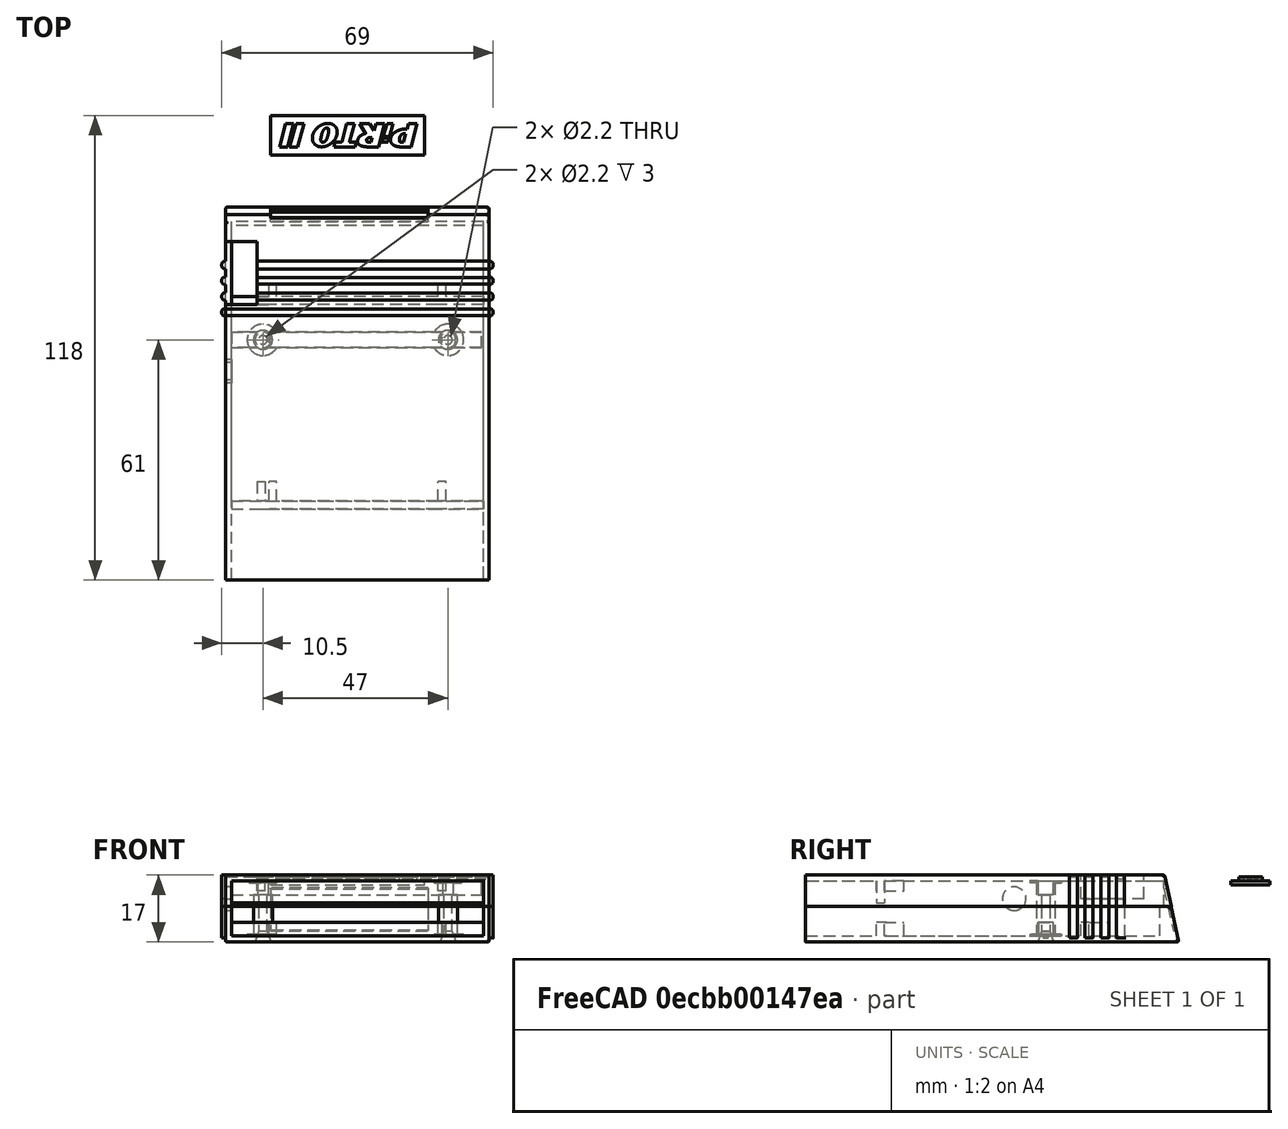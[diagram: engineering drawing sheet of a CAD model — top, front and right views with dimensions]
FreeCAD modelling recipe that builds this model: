
FCSTD DOCUMENT  (FreeCAD 0.21R33771 (Git))
Label: PiRTOII_Cart
License: All rights reserved
LicenseURL: http://en.wikipedia.org/wiki/All_rights_reserved
objects: Part::Cylinder×33, Part::MultiFuse×26, Part::Box×19, Part::Cut×17, Part::Fillet×8, Mesh::Feature×3, Part::Cone×2, Part::Part2DObjectPython×1, Part::Extrusion×1
note: 107 computed .brp shape members not serialized (recipe doc carries the construction recipe); baked Part::Feature solids carry a one-line shape summary decoded from their .brp

FEATURE [Part::Cylinder] Cylinder  label="Cilindro"
  Angle = 360
  AttacherType = Attacher::AttachEngine3D
  FirstAngle = 0
  Height = 1
  Placement = pos=(52.5,43,0) rot=(0,0,1;0rad)
  Radius = 4
  SecondAngle = 0
FEATURE [Part::Cylinder] Cylinder001  label="Cilindro001"
  Angle = 360
  AttacherType = Attacher::AttachEngine3D
  FirstAngle = 0
  Height = 1
  Placement = pos=(13.5,43,0) rot=(0,0,1;0rad)
  Radius = 4
  SecondAngle = 0
FEATURE [Part::Box] Box  label="Base_int"
  AttacherType = Attacher::AttachEngine3D
  Height = 10
  Length = 64
  Placement = pos=(1.5,0,0.5) rot=(0,0,1;0rad)
  Width = 90
FEATURE [Part::Box] Box001  label="Base_ext"
  AttacherType = Attacher::AttachEngine3D
  Height = 9
  Length = 67
  Placement = pos=(0,0,-1) rot=(0,0,1;0rad)
  Width = 95
FEATURE [Part::Cut] Cut  label="BaseVuota"
  Base = -> Box001
  Tool = -> Box
FEATURE [Part::Box] Box002  label="Cubo"
  AttacherType = Attacher::AttachEngine3D
  Height = 4
  Length = 66
  Placement = pos=(0,18,0) rot=(0,0,1;0rad)
  Width = 2
FEATURE [Part::Box] Box003  label="Cubo001"
  AttacherType = Attacher::AttachEngine3D
  Height = 4
  Length = 2
  Placement = pos=(11,18,0) rot=(0,0,1;0rad)
  Width = 7
FEATURE [Part::Box] Box004  label="Cubo002"
  AttacherType = Attacher::AttachEngine3D
  Height = 4
  Length = 2
  Placement = pos=(54,18,0) rot=(0,0,1;0rad)
  Width = 7
FEATURE [Part::MultiFuse] Fusion  label="Holder"
  Shapes = -> [Box004,Box003,Box002]
FEATURE [Part::Cylinder] Cylinder002  label="Cilindro002"
  Angle = 360
  AttacherType = Attacher::AttachEngine3D
  FirstAngle = 0
  Height = 8
  Placement = pos=(52.5,43,0) rot=(0,0,1;0rad)
  Radius = 2.4
  SecondAngle = 0
FEATURE [Part::Cylinder] Cylinder003  label="Cilindro003"
  Angle = 360
  AttacherType = Attacher::AttachEngine3D
  FirstAngle = 0
  Height = 8
  Placement = pos=(13.5,43,0) rot=(0,0,1;0rad)
  Radius = 2.4
  SecondAngle = 0
FEATURE [Part::MultiFuse] Fusion001
  Placement = pos=(-4,18,0) rot=(0,0,1;0rad)
  Shapes = -> [Cylinder003,Cylinder001]
FEATURE [Part::Box] Box005  label="apertura"
  AttacherType = Attacher::AttachEngine3D
  Height = 7
  Length = 18
  Placement = pos=(-10,70,10) rot=(0,0,1;0rad)
  Width = 16
FEATURE [Part::Cut] Cut001
  Base = -> Cut
  Tool = -> Box005
FEATURE [Part::Box] Box006  label="Taglio"
  AttacherType = Attacher::AttachEngine3D
  Height = 30
  Length = 72
  Placement = pos=(0,95,-2) rot=(1,0,0;0.20944rad)
  Width = 30
FEATURE [Part::Cut] Cut002  label="Base2"
  Base = -> Cut001
  Tool = -> Box006
FEATURE [Part::Cylinder] Cylinder004  label="Cyl1"
  Angle = 360
  AttacherType = Attacher::AttachEngine3D
  FirstAngle = 0
  Height = 8
  Placement = pos=(67,80,0) rot=(0,0,1;0rad)
  Radius = 1
  SecondAngle = 0
FEATURE [Part::Cylinder] Cylinder005  label="Cyl002"
  Angle = 360
  AttacherType = Attacher::AttachEngine3D
  FirstAngle = 0
  Height = 8
  Placement = pos=(67,84,0) rot=(0,0,1;0rad)
  Radius = 1
  SecondAngle = 0
FEATURE [Part::Cylinder] Cylinder006  label="Cyl003"
  Angle = 360
  AttacherType = Attacher::AttachEngine3D
  FirstAngle = 0
  Height = 8
  Placement = pos=(67,88,0) rot=(0,0,1;0rad)
  Radius = 1
  SecondAngle = 0
FEATURE [Part::Cylinder] Cylinder007  label="Cyl004"
  Angle = 360
  AttacherType = Attacher::AttachEngine3D
  FirstAngle = 0
  Height = 8
  Placement = pos=(67,76,0) rot=(0,0,1;0rad)
  Radius = 1
  SecondAngle = 0
FEATURE [Part::MultiFuse] Fusion004  label="ImpDX"
  Placement = pos=(0,-8,0) rot=(0,0,1;0rad)
  Shapes = -> [Cylinder004,Cylinder005,Cylinder006,Cylinder007]
FEATURE [Part::MultiFuse] Fusion005  label="Bot1"
  Shapes = -> [Fusion004,Cut002,Fusion]
FEATURE [Part::Fillet] Fillet  label="Base1"
  Base = -> Fusion005
  Edges = 2 edges r=0.6: [Edge22,Edge63]
FEATURE [Part::Box] Box007  label="Top_ext"
  AttacherType = Attacher::AttachEngine3D
  Height = 8
  Length = 67
  Placement = pos=(0,0,8) rot=(0,0,1;0rad)
  Width = 93
FEATURE [Part::Box] Box008  label="Top_int"
  AttacherType = Attacher::AttachEngine3D
  Height = 9
  Length = 64
  Placement = pos=(1.5,0,5.5) rot=(0,0,1;0rad)
  Width = 91
FEATURE [Part::Cut] Cut003
  Base = -> Box007
  Tool = -> Box008
FEATURE [Part::Cylinder] Cylinder008  label="Cyl005"
  Angle = 360
  AttacherType = Attacher::AttachEngine3D
  FirstAngle = 0
  Height = 8
  Placement = pos=(67,80,8) rot=(0,0,1;0rad)
  Radius = 1
  SecondAngle = 0
FEATURE [Part::Cylinder] Cylinder009  label="Cyl006"
  Angle = 360
  AttacherType = Attacher::AttachEngine3D
  FirstAngle = 0
  Height = 8
  Placement = pos=(67,84,8) rot=(0,0,1;0rad)
  Radius = 1
  SecondAngle = 0
FEATURE [Part::Cylinder] Cylinder010  label="Cyl007"
  Angle = 360
  AttacherType = Attacher::AttachEngine3D
  FirstAngle = 0
  Height = 8
  Placement = pos=(67,88,8) rot=(0,0,1;0rad)
  Radius = 1
  SecondAngle = 0
FEATURE [Part::Cylinder] Cylinder011  label="Cyl008"
  Angle = 360
  AttacherType = Attacher::AttachEngine3D
  FirstAngle = 0
  Height = 8
  Placement = pos=(67,76,8) rot=(0,0,1;0rad)
  Radius = 1
  SecondAngle = 0
FEATURE [Part::MultiFuse] Fusion006  label="ImpDX001"
  Placement = pos=(0,-8,0) rot=(0,0,1;0rad)
  Shapes = -> [Cylinder008,Cylinder009,Cylinder010,Cylinder011]
FEATURE [Part::Cylinder] Cylinder012  label="Cyl009"
  Angle = 360
  AttacherType = Attacher::AttachEngine3D
  FirstAngle = 0
  Height = 8
  Placement = pos=(-1,80,8) rot=(0,0,1;0rad)
  Radius = 1
  SecondAngle = 0
FEATURE [Part::Cylinder] Cylinder013  label="Cyl010"
  Angle = 360
  AttacherType = Attacher::AttachEngine3D
  FirstAngle = 0
  Height = 8
  Placement = pos=(-1,84,8) rot=(0,0,1;0rad)
  Radius = 1
  SecondAngle = 0
FEATURE [Part::Cylinder] Cylinder014  label="Cyl011"
  Angle = 360
  AttacherType = Attacher::AttachEngine3D
  FirstAngle = 0
  Height = 8
  Placement = pos=(-1,88,8) rot=(0,0,1;0rad)
  Radius = 1
  SecondAngle = 0
FEATURE [Part::Cylinder] Cylinder015  label="Cyl012"
  Angle = 360
  AttacherType = Attacher::AttachEngine3D
  FirstAngle = 0
  Height = 8
  Placement = pos=(-1,76,8) rot=(0,0,1;0rad)
  Radius = 1
  SecondAngle = 0
FEATURE [Part::MultiFuse] Fusion007  label="ImpSX"
  Placement = pos=(1,-8,0) rot=(0,0,1;0rad)
  Shapes = -> [Cylinder012,Cylinder013,Cylinder014,Cylinder015]
FEATURE [Part::MultiFuse] Fusion008
  Shapes = -> [Fusion007,Cut003]
FEATURE [Part::MultiFuse] Fusion009
  Shapes = -> [Fusion008,Fusion006]
FEATURE [Part::Cut] Cut004
  Base = -> Fusion009
  Tool = -> Box005
FEATURE [Part::Cut] Cut005
  Base = -> Cut004
  Tool = -> Box006
FEATURE [Part::Cylinder] Cylinder016  label="Cilindro004"
  Angle = 360
  AttacherType = Attacher::AttachEngine3D
  FirstAngle = 0
  Height = 2
  Placement = pos=(52.5,43,14) rot=(0,0,1;0rad)
  Radius = 4
  SecondAngle = 0
FEATURE [Part::Cylinder] Cylinder018  label="Cilindro006"
  Angle = 360
  AttacherType = Attacher::AttachEngine3D
  FirstAngle = 0
  Height = 8
  Placement = pos=(52.5,43,8) rot=(0,0,1;0rad)
  Radius = 2.4
  SecondAngle = 0
FEATURE [Part::Cylinder] Cylinder020  label="Cilindro008"
  Angle = 360
  AttacherType = Attacher::AttachEngine3D
  FirstAngle = 0
  Height = 5
  Placement = pos=(52.5,43,8) rot=(0,0,1;0rad)
  Radius = 1.1
  SecondAngle = 0
FEATURE [Part::Cut] Cut006
  Base = -> Cylinder018
  Tool = -> Cylinder020
FEATURE [Part::MultiFuse] Fusion013  label="PernoUpDx"
  Placement = pos=(4,0,0) rot=(0,0,1;0rad)
  Shapes = -> [Cylinder016,Cut006]
FEATURE [Part::Cylinder] Cylinder021  label="Cilindro009"
  Angle = 360
  AttacherType = Attacher::AttachEngine3D
  FirstAngle = 0
  Height = 2
  Placement = pos=(13.5,43,14) rot=(0,0,1;0rad)
  Radius = 4
  SecondAngle = 0
FEATURE [Part::Cylinder] Cylinder022  label="Cilindro010"
  Angle = 360
  AttacherType = Attacher::AttachEngine3D
  FirstAngle = 0
  Height = 8
  Placement = pos=(13.5,43,8) rot=(0,0,1;0rad)
  Radius = 2.4
  SecondAngle = 0
FEATURE [Part::Cylinder] Cylinder023  label="Cilindro011"
  Angle = 360
  AttacherType = Attacher::AttachEngine3D
  FirstAngle = 0
  Height = 5
  Placement = pos=(13.5,43,8) rot=(0,0,1;0rad)
  Radius = 1.1
  SecondAngle = 0
FEATURE [Part::Cut] Cut007
  Base = -> Cylinder022
  Tool = -> Cylinder023
FEATURE [Part::MultiFuse] Fusion014  label="PernoUpSx"
  Placement = pos=(-4,0,0) rot=(0,0,1;0rad)
  Shapes = -> [Cylinder021,Cut007]
FEATURE [Part::MultiFuse] Fusion015  label="PerniUp"
  Placement = pos=(0,18,0) rot=(0,0,1;0rad)
  Shapes = -> [Fusion014,Fusion013]
FEATURE [Part::Box] Box009  label="Cubo003"
  AttacherType = Attacher::AttachEngine3D
  Height = 6
  Length = 65
  Placement = pos=(0.5,12,9) rot=(0,0,1;0rad)
  Width = 2
FEATURE [Part::Box] Box010  label="Cubo004"
  AttacherType = Attacher::AttachEngine3D
  Height = 4
  Length = 2
  Placement = pos=(8,12,12) rot=(0,0,1;0rad)
  Width = 7
FEATURE [Part::Box] Box011  label="Cubo005"
  AttacherType = Attacher::AttachEngine3D
  Height = 4
  Length = 2
  Placement = pos=(54,12,12) rot=(0,0,1;0rad)
  Width = 7
FEATURE [Part::MultiFuse] Fusion016  label="HolderUp"
  Placement = pos=(0,6,0) rot=(0,0,1;0rad)
  Shapes = -> [Box011,Box010,Box009]
FEATURE [Part::Part2DObjectPython] ShapeString  # Draft 2D object (typed FeaturePython)
  FontFile = <userpath>/Documents/Retrocomputer/Intellivision/3DModel/sfintell.ttf
  MakeFace = true
  Size = 3.5
  String = PiRTO II
  Tracking = 0
FEATURE [Part::Extrusion] Extrude  label="Scritta"
  Base = -> ShapeString
  Dir = (0,0,1)
  DirMode = 2
  FaceMakerClass = Part::FaceMakerBullseye
  LengthFwd = 2
  LengthRev = 0
  Placement = pos=(49,116,13.6) rot=(0,0,1;3.14159rad)
  Solid = false
  Symmetric = false
FEATURE [Part::Cylinder] Cylinder024  label="Cilindro012"
  Angle = 360
  AttacherType = Attacher::AttachEngine3D
  FirstAngle = 0
  Height = 22
  Placement = pos=(56.5,61,-10) rot=(0,0,1;0rad)
  Radius = 1.1
  SecondAngle = 0
FEATURE [Part::MultiFuse] Fusion019
  Placement = pos=(4,18,0) rot=(0,0,1;0rad)
  Shapes = -> [Cylinder,Cylinder002]
FEATURE [Part::Cylinder] Cylinder025  label="Cilindro013"
  Angle = 360
  AttacherType = Attacher::AttachEngine3D
  FirstAngle = 0
  Height = 22
  Placement = pos=(9.5,61,-10) rot=(0,0,1;0rad)
  Radius = 1.1
  SecondAngle = 0
FEATURE [Part::MultiFuse] Fusion020
  Shapes = -> [Fillet,Fusion019,Fusion001]
FEATURE [Part::Cut] Cut010
  Base = -> Fusion020
  Tool = -> Cylinder024
FEATURE [Part::Cut] Cut011
  Base = -> Cut010
  Tool = -> Cylinder025
FEATURE [Part::Cone] Cone  label="Cono"
  Angle = 360
  AttacherType = Attacher::AttachEngine3D
  Height = 3
  Placement = pos=(9.5,61,2) rot=(1,0,0;3.14159rad)
  Radius1 = 1
  Radius2 = 2
FEATURE [Part::Cone] Cone001  label="Cono001"
  Angle = 360
  AttacherType = Attacher::AttachEngine3D
  Height = 3
  Placement = pos=(56.5,61,2) rot=(1,0,0;3.14159rad)
  Radius1 = 1
  Radius2 = 2
FEATURE [Part::Cut] Cut012
  Base = -> Cut011
  Tool = -> Cone
FEATURE [Part::Cut] Cut013
  Base = -> Cut012
  Tool = -> Cone001
FEATURE [Part::Box] Box013  label="Cubo007"
  AttacherType = Attacher::AttachEngine3D
  Height = 4
  Length = 44
  Placement = pos=(11,59,0) rot=(0,0,1;0rad)
  Width = 4
FEATURE [Part::Cylinder] Cylinder026  label="Cilindro014"
  Angle = 360
  AttacherType = Attacher::AttachEngine3D
  FirstAngle = 0
  Height = 67
  Placement = pos=(0,84,17) rot=(0,1,0;1.5708rad)
  Radius = 1
  SecondAngle = 0
FEATURE [Part::Cylinder] Cylinder027  label="Cilindro015"
  Angle = 360
  AttacherType = Attacher::AttachEngine3D
  FirstAngle = 0
  Height = 67
  Placement = pos=(0,80,17) rot=(0,1,0;1.5708rad)
  Radius = 1
  SecondAngle = 0
FEATURE [Part::Cylinder] Cylinder028  label="Cilindro016"
  Angle = 360
  AttacherType = Attacher::AttachEngine3D
  FirstAngle = 0
  Height = 67
  Placement = pos=(0,76,17) rot=(0,1,0;1.5708rad)
  Radius = 1
  SecondAngle = 0
FEATURE [Part::MultiFuse] Fusion023  label="CylTop1"
  Placement = pos=(0,-8,-1) rot=(0,0,1;0rad)
  Shapes = -> [Cylinder026,Cylinder027,Cylinder028]
FEATURE [Part::Cylinder] Cylinder029  label="Cyl013"
  Angle = 360
  AttacherType = Attacher::AttachEngine3D
  FirstAngle = 0
  Height = 8
  Placement = pos=(-1,80,0) rot=(0,0,1;0rad)
  Radius = 1
  SecondAngle = 0
FEATURE [Part::Cylinder] Cylinder030  label="Cyl014"
  Angle = 360
  AttacherType = Attacher::AttachEngine3D
  FirstAngle = 0
  Height = 8
  Placement = pos=(-1,84,0) rot=(0,0,1;0rad)
  Radius = 1
  SecondAngle = 0
FEATURE [Part::Cylinder] Cylinder031  label="Cyl015"
  Angle = 360
  AttacherType = Attacher::AttachEngine3D
  FirstAngle = 0
  Height = 8
  Placement = pos=(-1,88,0) rot=(0,0,1;0rad)
  Radius = 1
  SecondAngle = 0
FEATURE [Part::Cylinder] Cylinder032  label="Cyl016"
  Angle = 360
  AttacherType = Attacher::AttachEngine3D
  FirstAngle = 0
  Height = 8
  Placement = pos=(-1,76,0) rot=(0,0,1;0rad)
  Radius = 1
  SecondAngle = 0
FEATURE [Part::MultiFuse] Fusion024  label="ImpSXBase"
  Placement = pos=(1,-8,0) rot=(0,0,1;0rad)
  Shapes = -> [Cylinder029,Cylinder030,Cylinder031,Cylinder032]
FEATURE [Part::Box] Box015  label="TaglioScritta"
  AttacherType = Attacher::AttachEngine3D
  Height = 2
  Length = 40
  Placement = pos=(11.5,91,12.5) rot=(-1,0,0;1.3439rad)
  Width = 11
FEATURE [Part::MultiFuse] Fusion026
  Shapes = -> [Cut013,Box013]
FEATURE [Part::Box] Box016  label="Cubo008"
  AttacherType = Attacher::AttachEngine3D
  Height = 4
  Length = 66
  Placement = pos=(0,18,0) rot=(0,0,1;0rad)
  Width = 2
FEATURE [Part::Box] Box017  label="Cubo009"
  AttacherType = Attacher::AttachEngine3D
  Height = 4
  Length = 2
  Placement = pos=(11,18,0) rot=(0,0,1;0rad)
  Width = 7
FEATURE [Part::Box] Box018  label="Cubo010"
  AttacherType = Attacher::AttachEngine3D
  Height = 4
  Length = 2
  Placement = pos=(54,18,0) rot=(0,0,1;0rad)
  Width = 7
FEATURE [Part::MultiFuse] Fusion028  label="Holder001"
  Placement = pos=(0,52,0) rot=(0,0,1;0rad)
  Shapes = -> [Box018,Box017,Box016]
FEATURE [Part::Cut] Cut022  label="Basex"
  Base = -> Fusion026
  Tool = -> Box015
FEATURE [Part::MultiFuse] Fusion030
  Shapes = -> [Fusion016,Cut005]
FEATURE [Part::MultiFuse] Fusion031
  Shapes = -> [Fusion015,Fusion030]
FEATURE [Part::MultiFuse] Fusion032  label="Basex001"
  Shapes = -> [Cut022,Fusion028]
FEATURE [Part::MultiFuse] Fusion033  label="Base005"
  Shapes = -> [Fusion024]
FEATURE [Part::Cylinder] Cylinder033  label="Cilindro017"
  Angle = 360
  AttacherType = Attacher::AttachEngine3D
  FirstAngle = 0
  Height = 67
  Placement = pos=(0,80,15.5) rot=(0,1,0;1.5708rad)
  Radius = 1
  SecondAngle = 0
FEATURE [Part::MultiFuse] Fusion034  label="CylTop"
  Placement = pos=(0,0,0.5) rot=(0,0,1;0rad)
  Shapes = -> [Fusion023,Cylinder033]
FEATURE [Part::Cylinder] Cylinder034  label="ForoReset"
  Angle = 360
  AttacherType = Attacher::AttachEngine3D
  FirstAngle = 0
  Height = 10
  Placement = pos=(-5,53,10) rot=(0,1,0;1.5708rad)
  Radius = 3
  SecondAngle = 0
FEATURE [Part::Cut] Cut023
  Base = -> Fusion031
  Tool = -> Fusion034
FEATURE [Part::MultiFuse] Fusion035
  Shapes = -> [Fusion033,Fusion032]
FEATURE [Part::Fillet] Fillet018
  Base = -> Fusion035
  Edges = 2 edges r=0.5: [Edge36,Edge95]
FEATURE [Part::Fillet] Fillet019  label="Base006"
  Base = -> Fillet018
  Edges = 1 edges r=0.4: [Edge1]
FEATURE [Part::Box] Box019  label="BaseScritta"
  AttacherType = Attacher::AttachEngine3D
  Height = 1
  Length = 39
  Placement = pos=(11.5,108,13.5) rot=(0,0,1;0rad)
  Width = 10
FEATURE [Part::MultiFuse] Fusion036  label="Logo"
  Shapes = -> [Box019,Extrude]
FEATURE [Mesh::Feature] Mesh  label="Logo (Meshed)"
  Placement = pos=(0.5,56,115) rot=(-1,0,0;1.36136rad)
FEATURE [Part::Cut] Cut026  label="Bot_tosmuss"
  Base = -> Fillet019
  Tool = -> Cylinder034
FEATURE [Part::Cut] Cut027
  Base = -> Cut023
  Tool = -> Cylinder034
FEATURE [Part::Cut] Cut028
  Base = -> Cut027
  Tool = -> Box015
FEATURE [Part::Fillet] Fillet020
  Base = -> Cut028
  Edges = 3 edges r=0.4: [Edge131,Edge166,Edge167]
FEATURE [Part::Fillet] Fillet022  label="Topx"
  Base = -> Fillet020
  Edges = 2 edges r=0.4: [Edge61,Edge140]
FEATURE [Part::Fillet] Fillet023  label="Bot"
  Base = -> Cut026
  Edges = 4 edges r=0.4: [Edge63,Edge105,Edge106,Edge133]
FEATURE [Part::Fillet] Fillet024
  Base = -> Fillet022
  Edges = 4 edges r=0.4: [Edge64,Edge69,Edge100,Edge104]
FEATURE [Part::Fillet] Fillet025  label="Top01"
  Base = -> Fillet024
  Edges = 1 edges r=0.4: [Edge42]
FEATURE [Mesh::Feature] Mesh002  label="Bot (Meshed)"
FEATURE [Part::Box] Box020  label="Cubo011"
  AttacherType = Attacher::AttachEngine3D
  Height = 5
  Length = 64
  Placement = pos=(1,59,11) rot=(0,0,1;0rad)
  Width = 4
FEATURE [Part::MultiFuse] Fusion037  label="Top"
  Shapes = -> [Fillet025,Box020]
FEATURE [Mesh::Feature] Mesh003  label="Top (Meshed)"
